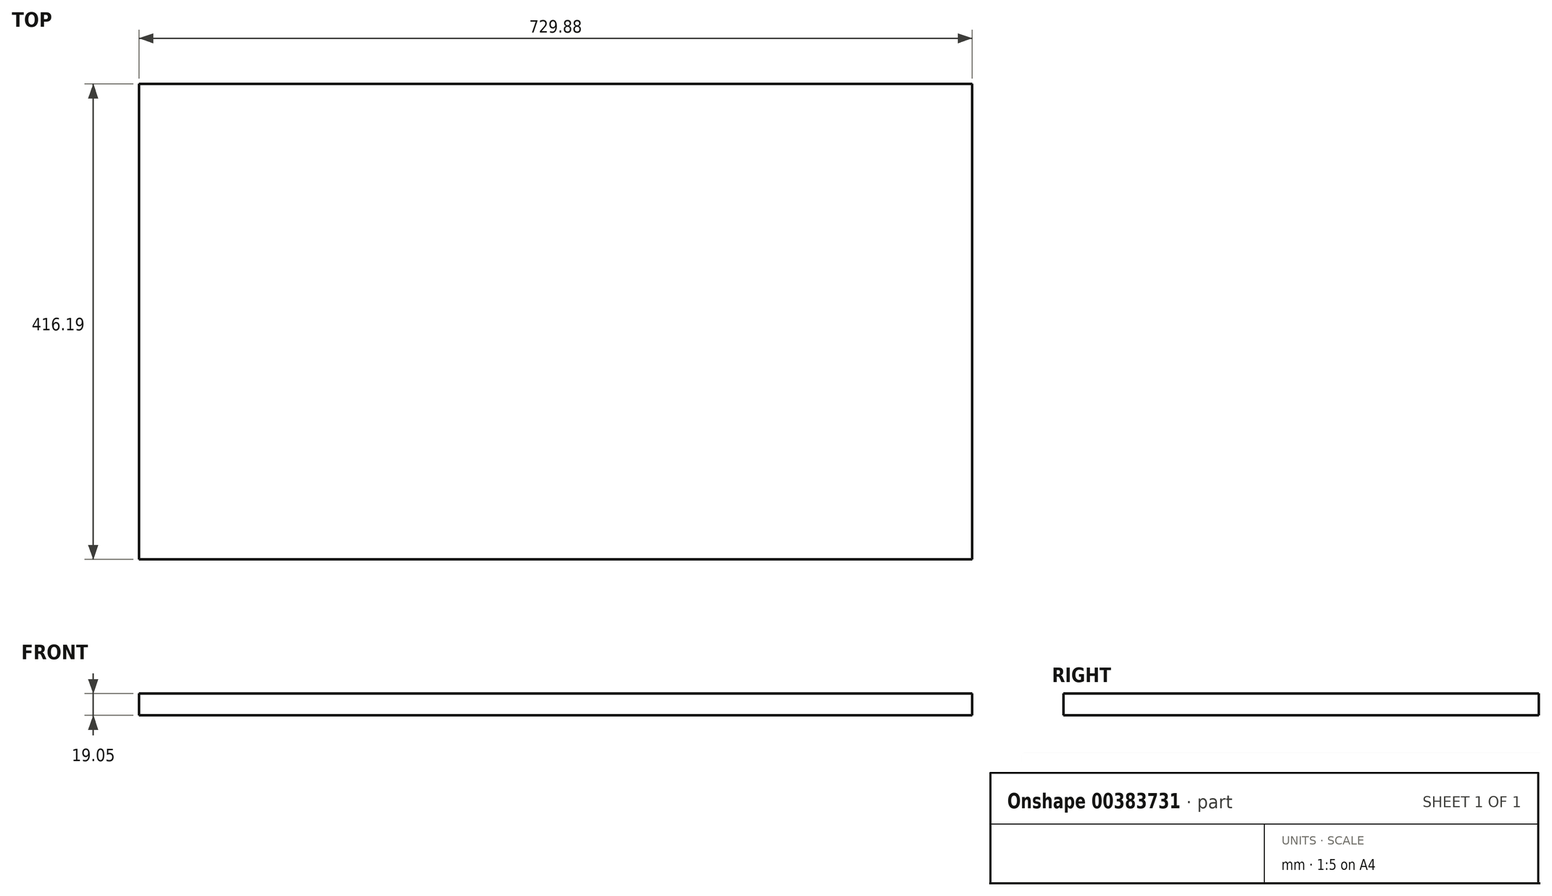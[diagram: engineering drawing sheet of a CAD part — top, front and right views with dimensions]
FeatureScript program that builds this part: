
annotation { "Feature Type Name" : "Feature", "Feature Type Description" : "" }
export const myFeature = defineFeature(function(context is Context, id is Id, definition is map)
    precondition{}
    {
        {
            var Q0;
            Q0=qCreatedBy(makeId("Top.planeOp"),FACE);
            var sketch = newSketch(context, id + "F0", { "sketchPlane" : qUnion([Q0])});
            skLineSegment(sketch, "E0.bottom", {"start": v(-376.42, -244.52) * mm, "end": v(353.46, -244.52) * mm});
            skLineSegment(sketch, "E0.top", {"start": v(-376.42, 171.67) * mm, "end": v(353.46, 171.67) * mm});
            skLineSegment(sketch, "E0.left", {"start": v(-376.42, -244.52) * mm, "end": v(-376.42, 171.67) * mm});
            skLineSegment(sketch, "E0.right", {"start": v(353.46, -244.52) * mm, "end": v(353.46, 171.67) * mm});
            skSolve(sketch);
        }
        {
            var Q0;
            Q0=makeQuery(id+"F0.imprint","IMPRINT",FACE,{"disambiguationData":[TD([[makeQuery(id+"F0.imprint","IMPRINT",EDGE,{"derivedFrom":sQuery(id+"F0.wireOp",EDGE,"E0.bottom")}),1.0]])]});
            extrude(context, id + "F1", {"entities" : qUnion([Q0]), "depth" : 19.05 * mm});
        }
    });
